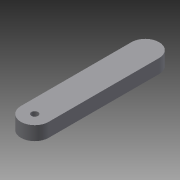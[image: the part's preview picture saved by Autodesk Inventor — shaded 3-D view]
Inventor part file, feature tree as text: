
AUTODESK INVENTOR PART (.ipt)
format: ipt  version: 2015 (Build 190159000, 159)  size: 74,752 bytes
history: native  units: in
note: dims shown in document units (in); Inventor stores cm internally (conversion verified against a paired STEP export)
features: extrude x1, sketch x1
ambient origin geometry x8: Origin, YZ Plane, XZ Plane, XY Plane, X Axis, Y Axis, Z Axis, Center Point
bodies: Solid1 (feature_tree)
feature tree (2):
  extrude  "Extrusion1"  Depth=0.5in
  sketch  "Sketch1"  dims[d0=2.0in d1=0.5in d2=0.25in d3=0.0in]
